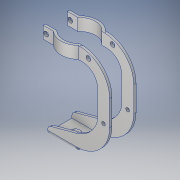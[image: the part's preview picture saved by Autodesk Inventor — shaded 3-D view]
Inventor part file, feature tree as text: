
AUTODESK INVENTOR PART (.ipt)
format: ipt  version: 2018 (Build 220112000, 112)  size: 322,048 bytes
history: native  units: in
note: dims shown in document units (in); Inventor stores cm internally (conversion verified against a paired STEP export)
features: extrude x10, sketch x10, fillet x5
ambient origin geometry x8: Origin, YZ Plane, XZ Plane, XY Plane, X Axis, Y Axis, Z Axis, Center Point
bodies: Solid1 (feature_tree)
feature tree (25):
  extrude  "Extrusion1"  Depth=0.438in
  extrude  "Extrusion2"  Depth=0.237in
  extrude  "Extrusion3"  Depth=0.0385in TaperAngle=0.0deg
  fillet  "Fillet1"  Radius=0.0385in
  fillet  "Fillet2"  Radius=0.0385in
  extrude  "Extrusion4"  TaperAngle=15.0deg  [1 undecoded]
  extrude  "Extrusion5"  Depth=0.0625in
  extrude  "Extrusion6"  Depth=0.0625in TaperAngle=0.0deg
  fillet  "Fillet3"  Radius=1.275in
  extrude  "Extrusion7"  Depth=0.5in
  fillet  "Fillet4"  Radius=0.2in
  fillet  "Fillet5"  Radius=0.5in
  extrude  "Extrusion11"  Depth=0.0625in
  extrude  "Extrusion10"  Depth=0.2in
  extrude  "Extrusion12"  Depth=0.25in
  sketch  "Sketch1"  dims[d0=0.4735in d1=0.438in]
  sketch  "Sketch2"  dims[d2=0.219in d3=0.237in]
  sketch  "Sketch3"  dims[d4=0.1565in d5=0.038in d6=0.0in d7=0.0385in d8=0.0385in]
  sketch  "Sketch4"  dims[d9=0.5in d10=0.0in d11=15.0deg]
  sketch  "Sketch5"  dims[d12=0.5in d13=0.0in d14=0.0625in]
  sketch  "Sketch6"  dims[d15=0.0625in d16=0.55in d17=0.0in d18=1.275in d19=0.0in]
  sketch  "Sketch7"  dims[d20=135.0deg d21=0.55in d22=0.2in d23=0.5in]
  sketch  "Sketch10"  dims[d24=1.275in d25=0.0in d26=0.0625in]
  sketch  "Sketch11"  dims[d27=0.2in d28=0.2in]
  sketch  "Sketch12"  dims[d29=0.9in d30=0.0in d31=0.25in d32=0.5in d45=0.05in d46=0.1in d47=0.1in d48=0.15in d49=0.1in d50=0.0in d51=0.078in d52=0.078in d53=0.06in d54=0.2in d55=0.0in d56=0.375in d57=0.225in d58=0.53in d59=0.0385in d60=0.039in d61=0.2in d62=0.0in d63=0.375in d64=0.225in d65=0.2in d66=0.0in]
note: 1 required parameter value undecoded (feature->parameter linkage not recoverable at this tier; creation-order binding heuristic only, values carry confidence <= 0.55)
